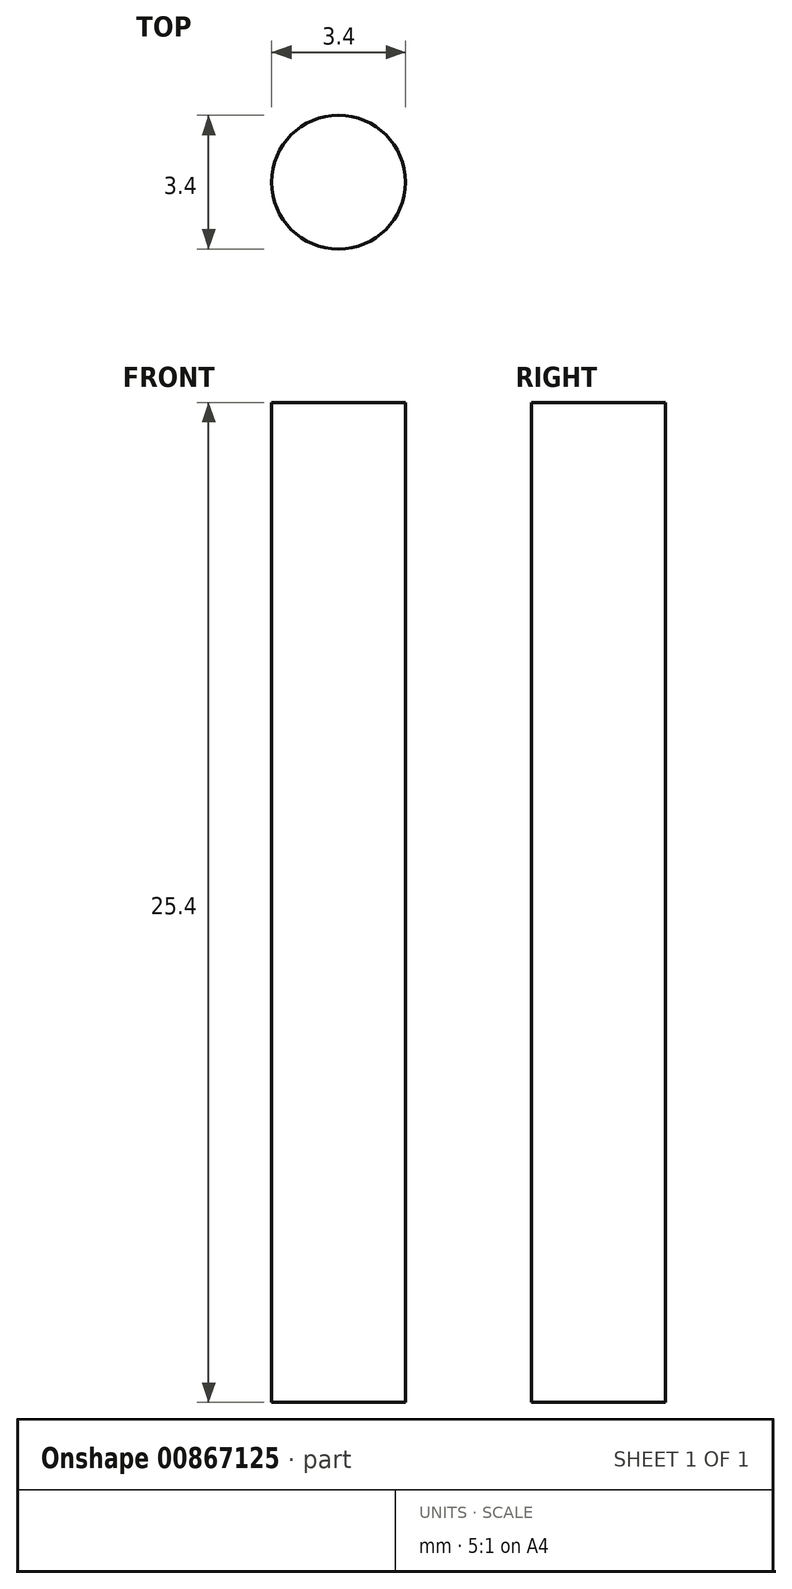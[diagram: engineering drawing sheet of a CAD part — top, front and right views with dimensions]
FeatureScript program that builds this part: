
annotation { "Feature Type Name" : "Feature", "Feature Type Description" : "" }
export const myFeature = defineFeature(function(context is Context, id is Id, definition is map)
    precondition{}
    {
        {
            var Q0;
            Q0=qCreatedBy(makeId("Top.planeOp"),FACE);
            var sketch = newSketch(context, id + "F0", { "sketchPlane" : qUnion([Q0])});
            skCircle(sketch, "E0", {"center": v(0, 0) * mm, "radius": 1.7 * mm});
            skSolve(sketch);
        }
        {
            var Q0;
            Q0=makeQuery(id+"F0.imprint","IMPRINT",FACE,{"disambiguationData":[TD([[makeQuery(id+"F0.imprint","IMPRINT",EDGE,{"derivedFrom":sQuery(id+"F0.wireOp",EDGE,"E0")}),1.0]])]});
            extrude(context, id + "F1", {"entities" : qUnion([Q0]), "depth" : 25.4 * mm, "offsetDistance" : 25.4 * mm});
        }
    });
